# Revit family: PV Systemlösung Typ 1+2 _Typ 2 für WR mit  MPP-Tracker
name_source: partatom
category: Generic Models
revit_build: Autodesk Revit 2015 (Build: 20140606_1530(x64)
units: mm (PartAtom-declared; Revit-internal decimal feet)

## types (3) — shared parameters
Diameter = 41 mm  [stored 0.134514 ft]
Diameter 1 = 36 mm
Height = 138 mm
Height 1 = 106 mm
Length = 285 mm  [stored 0.935039 ft]
Manufacturer = OBO Bettermann
Material = OBO PP
Material 2 = PC
Material 3 = OBO TPE
URL = http://www.obo-bettermann.com
Width = 201 mm

## per-type parameters (varying)
| type | GTIN | Manufacturer Art.No. |
| VG-BCPV900K 22 | 4012196190263 | 5088566 |
| VG-CPV1000K 22 | 4012196329854 | 5088568 |
| VG-BCPV 900KS 11 | 4012196410873 | 5088581 |

note: column(s) folded — value = type name in every type: Article Type

note: [stored X ft] marks values corroborated as IEEE doubles in the binary element streams (Revit-internal decimal feet)

## geometry (parser evidence)
native form markers: Sweep x2
no freeform markers — native parametric forms only
